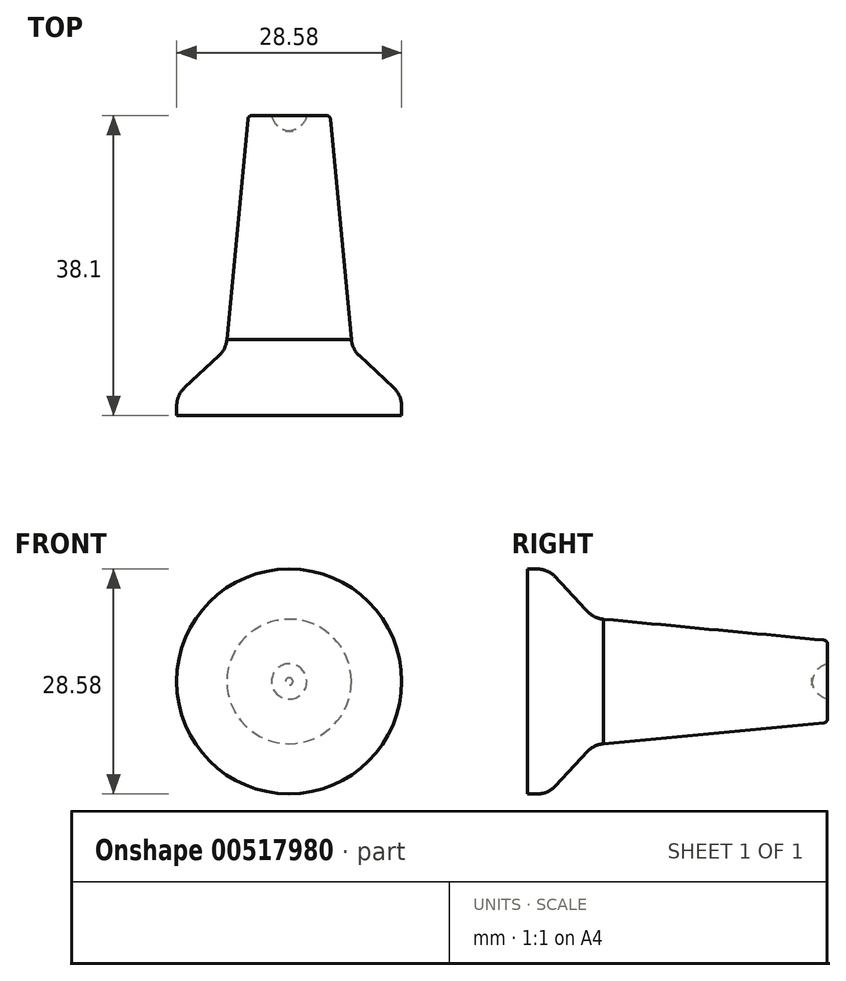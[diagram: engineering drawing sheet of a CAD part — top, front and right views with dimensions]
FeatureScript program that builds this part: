
annotation { "Feature Type Name" : "Feature", "Feature Type Description" : "" }
export const myFeature = defineFeature(function(context is Context, id is Id, definition is map)
    precondition{}
    {
        {
            var Q0;
            Q0=qCreatedBy(makeId("Top.planeOp"),FACE);
            var sketch = newSketch(context, id + "F0", { "sketchPlane" : qUnion([Q0])});
            skLineSegment(sketch, "E0", {"start": v(0, 27.2) * mm, "end": v(0, -11.4) * mm});
            skLineSegment(sketch, "E1", {"start": v(0, 27.2) * mm, "end": v(0, 39.59) * mm});
            skPoint(sketch, "E2.visualSharp", {"position": v(-3.81, 27.92) * mm});
            skLineSegment(sketch, "E3", {"start": v(-14.29, -8.94) * mm, "end": v(0, -8.94) * mm});
            skPoint(sketch, "E4.visualSharp", {"position": v(-3.18, 29.86) * mm});
            skLineSegment(sketch, "E5", {"start": v(-14.29, -8.94) * mm, "end": v(-14.29, -7.73) * mm});
            skLineSegment(sketch, "E6", {"start": v(-13.27, -5.4) * mm, "end": v(-8.91, -1.35) * mm});
            skPoint(sketch, "E7.visualSharp", {"position": v(-14.29, -6.35) * mm});
            skArc(sketch, "E7.filletArc", {"start": v(-13.27, -5.4) * mm, "mid": v(-14.02, -6.46) * mm, "end": v(-14.29, -7.73) * mm});
            skPoint(sketch, "E8.visualSharp", {"position": v(-8, -0.51) * mm});
            skArc(sketch, "E8.filletArc", {"start": v(-8.91, -1.35) * mm, "mid": v(-8.21, -0.41) * mm, "end": v(-7.9, 0.72) * mm});
            skLineSegment(sketch, "E9", {"start": v(-4.74, 29.16) * mm, "end": v(-2.24, 29.16) * mm});
            skArc(sketch, "E10", {"start": v(-2.24, 29.16) * mm, "mid": v(-1.44, 27.81) * mm, "end": v(0, 27.2) * mm});
            skLineSegment(sketch, "E11", {"start": v(-7.9, 0.72) * mm, "end": v(-5.25, 28.7) * mm});
            skPoint(sketch, "E12.visualSharp", {"position": v(-5.2, 29.16) * mm});
            skArc(sketch, "E12.filletArc", {"start": v(-4.74, 29.16) * mm, "mid": v(-5.08, 29.02) * mm, "end": v(-5.25, 28.7) * mm});
            skSolve(sketch);
        }
        {
            var Q0;
            Q0 = qSketchRegion(id + "F0", true);
            var Q1;
            Q1=sQuery(id+"F0.wireOp",EDGE,"E0");
            revolve(context, id + "F1", {"entities" : qUnion([Q0]), "axis" : qUnion([Q1]), "revolveType" : RevolveType.FULL});
        }
    });
